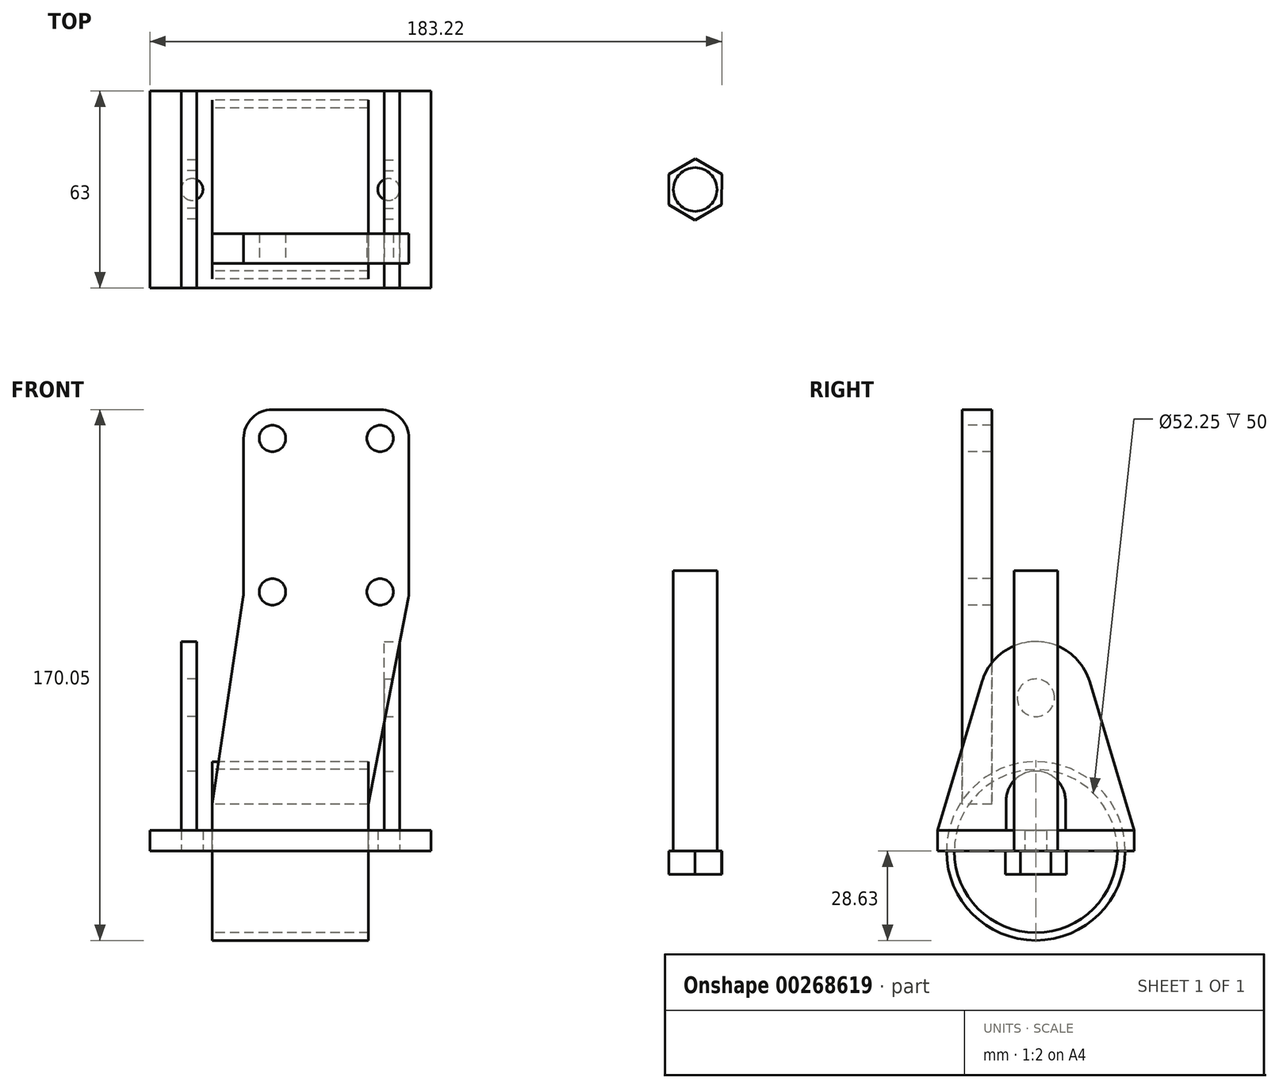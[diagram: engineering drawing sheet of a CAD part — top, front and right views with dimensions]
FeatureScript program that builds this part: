
annotation { "Feature Type Name" : "Feature", "Feature Type Description" : "" }
export const myFeature = defineFeature(function(context is Context, id is Id, definition is map)
    precondition{}
    {
        {
            var Q0;
            Q0=qCreatedBy(makeId("Top.planeOp"),FACE);
            var sketch = newSketch(context, id + "F0", { "sketchPlane" : qUnion([Q0])});
            skLineSegment(sketch, "E0.bottom", {"start": v(45, 31.5) * mm, "end": v(-45, 31.5) * mm});
            skLineSegment(sketch, "E0.top", {"start": v(45, -31.5) * mm, "end": v(-45, -31.5) * mm});
            skLineSegment(sketch, "E0.left", {"start": v(45, 31.5) * mm, "end": v(45, -31.5) * mm});
            skLineSegment(sketch, "E0.right", {"start": v(-45, 31.5) * mm, "end": v(-45, -31.5) * mm});
            skPoint(sketch, "E0.middle", {"position": v(0, 0) * mm});
            skCircle(sketch, "E1", {"center": v(31.5, 0) * mm, "radius": 3.5 * mm});
            skCircle(sketch, "E2.MirrorC", {"center": v(-31.5, 0) * mm, "radius": 3.5 * mm});
            skSolve(sketch);
        }
        {
            var Q0;
            Q0=makeQuery(id+"F0.imprint","IMPRINT",FACE,{"disambiguationData":[TD([[makeQuery(id+"F0.imprint","IMPRINT",EDGE,{"derivedFrom":sQuery(id+"F0.wireOp",EDGE,"E0.bottom")}),1.0]])]});
            extrude(context, id + "F1", {"entities" : qUnion([Q0]), "depth" : 6.6 * mm});
        }
        {
            var Q0;
            Q0=makeQuery(id+"F1.opExtrude","SWEPT_FACE",FACE,{"disambiguationData":[OSD([sQuery(id+"F0.wireOp",EDGE,"E0.right")])]});
            cPlane(context, id + "F2", {"entities" : qUnion([Q0]), "cplaneType" : CPlaneType.OFFSET, "offset" : 10 * mm, "oppositeDirection" : true, "width" : 150 * mm, "height" : 150 * mm});
        }
        {
            var Q0;
            Q0=qCreatedBy(id+"F2.planeOp",FACE);
            var sketch = newSketch(context, id + "F3", { "sketchPlane" : qUnion([Q0])});
            skLineSegment(sketch, "E3", {"start": v(-31.5, 6.6) * mm, "end": v(-9.5, 6.6) * mm});
            skCircle(sketch, "E4", {"center": v(0, 49.1) * mm, "radius": 6 * mm});
            skArc(sketch, "E5", {"start": v(17.25, 54.26) * mm, "mid": v(0, 67.1) * mm, "end": v(-17.25, 54.26) * mm});
            skLineSegment(sketch, "E6", {"start": v(31.5, 6.6) * mm, "end": v(17.25, 54.26) * mm});
            skLineSegment(sketch, "E7", {"start": v(-31.5, 6.6) * mm, "end": v(-17.25, 54.26) * mm});
            skLineSegment(sketch, "E8.left", {"start": v(9.5, 16.1) * mm, "end": v(9.5, 6.6) * mm});
            skLineSegment(sketch, "E8.right", {"start": v(-9.5, 16.1) * mm, "end": v(-9.5, 6.6) * mm});
            skPoint(sketch, "E8.middle", {"position": v(0, 6.6) * mm});
            skArc(sketch, "E9", {"start": v(9.5, 16.1) * mm, "mid": v(0, 25.6) * mm, "end": v(-9.5, 16.1) * mm});
            skLineSegment(sketch, "E10.trimOffspring", {"start": v(9.5, 6.6) * mm, "end": v(31.5, 6.6) * mm});
            skSolve(sketch);
        }
        {
            var Q0;
            Q0=makeQuery(id+"F3.imprint","IMPRINT",FACE,{"disambiguationData":[TD([[makeQuery(id+"F3.imprint","IMPRINT",EDGE,{"derivedFrom":sQuery(id+"F3.wireOp",EDGE,"E3")}),1.0]])]});
            extrude(context, id + "F4", {"entities" : qUnion([Q0]), "operationType" : NewBodyOperationType.ADD, "oppositeDirection" : true, "depth" : 5 * mm});
        }
        {
            var Q0;
            Q0=makeQuery(id+"F1.opExtrude","SWEPT_BODY",BODY,{"disambiguationData":[OSD([sQuery(id+"F0.wireOp",EDGE,"E0.bottom"),sQuery(id+"F0.wireOp",EDGE,"E0.top"),sQuery(id+"F0.wireOp",EDGE,"E0.left"),sQuery(id+"F0.wireOp",EDGE,"E0.right"),sQuery(id+"F0.wireOp",EDGE,"E1"),sQuery(id+"F0.wireOp",EDGE,"E2.MirrorC")])]});
            var Q1;
            Q1=qCreatedBy(makeId("Right.planeOp"),FACE);
            mirror(context, id + "F5", {"operationType" : NewBodyOperationType.ADD, "entities" : qUnion([Q0]), "mirrorPlane" : qUnion([Q1])});
        }
        {
            var Q0;
            Q0=qCreatedBy(makeId("Right.planeOp"),FACE);
            var sketch = newSketch(context, id + "F6", { "sketchPlane" : qUnion([Q0])});
            skCircle(sketch, "E11", {"center": v(0, 0) * mm, "radius": 28.62 * mm});
            skCircle(sketch, "E12", {"center": v(0, 0) * mm, "radius": 26.12 * mm});
            skSolve(sketch);
        }
        {
            var Q0;
            Q0=makeQuery(id+"F6.imprint","IMPRINT",FACE,{"disambiguationData":[TD([[makeQuery(id+"F6.imprint","IMPRINT",EDGE,{"derivedFrom":sQuery(id+"F6.wireOp",EDGE,"E11")}),1.0]])]});
            extrude(context, id + "F7", {"entities" : qUnion([Q0]), "endBound" : BoundingType.SYMMETRIC, "depth" : 50 * mm});
        }
        {
            var Q0;
            Q0=qCreatedBy(makeId("Front.planeOp"),FACE);
            cPlane(context, id + "F8", {"entities" : qUnion([Q0]), "cplaneType" : CPlaneType.OFFSET, "offset" : 23.62 * mm, "width" : 150 * mm, "height" : 150 * mm});
        }
        {
            var Q0;
            Q0=qCreatedBy(id+"F8.planeOp",FACE);
            var sketch = newSketch(context, id + "F9", { "sketchPlane" : qUnion([Q0])});
            skLineSegment(sketch, "E13.top", {"start": v(-5.75, 141.42) * mm, "end": v(28.75, 141.42) * mm});
            skLineSegment(sketch, "E13.left", {"start": v(-15, 82.91) * mm, "end": v(-15, 132.17) * mm});
            skLineSegment(sketch, "E13.right", {"start": v(38, 83.13) * mm, "end": v(38, 132.17) * mm});
            skPoint(sketch, "E13.middle", {"position": v(11.5, 111.8) * mm});
            skLineSegment(sketch, "E14", {"start": v(37.82, 81.23) * mm, "end": v(25, 15) * mm});
            skLineSegment(sketch, "E15", {"start": v(25, 15) * mm, "end": v(-25, 15) * mm});
            skLineSegment(sketch, "E16", {"start": v(-25, 15) * mm, "end": v(-15.1, 81.44) * mm});
            skPoint(sketch, "E17.visualSharp", {"position": v(38, 82.17) * mm});
            skArc(sketch, "E17.filletArc", {"start": v(37.82, 81.23) * mm, "mid": v(37.95, 82.18) * mm, "end": v(38, 83.13) * mm});
            skPoint(sketch, "E18.visualSharp", {"position": v(-15, 82.17) * mm});
            skArc(sketch, "E18.filletArc", {"start": v(-15.1, 81.44) * mm, "mid": v(-15.03, 82.17) * mm, "end": v(-15, 82.91) * mm});
            skCircle(sketch, "E19", {"center": v(28.75, 132.17) * mm, "radius": 4.25 * mm});
            skCircle(sketch, "E20", {"center": v(-5.75, 132.17) * mm, "radius": 4.25 * mm});
            skCircle(sketch, "E21", {"center": v(28.75, 83.02) * mm, "radius": 4.25 * mm});
            skCircle(sketch, "E22", {"center": v(-5.75, 83.02) * mm, "radius": 4.25 * mm});
            skPoint(sketch, "E23.visualSharp", {"position": v(-15, 141.42) * mm});
            skArc(sketch, "E23.filletArc", {"start": v(-5.75, 141.42) * mm, "mid": v(-12.3, 138.71) * mm, "end": v(-15, 132.17) * mm});
            skPoint(sketch, "E24.visualSharp", {"position": v(38, 141.42) * mm});
            skArc(sketch, "E24.filletArc", {"start": v(38, 132.17) * mm, "mid": v(35.3, 138.71) * mm, "end": v(28.75, 141.42) * mm});
            skSolve(sketch);
        }
        {
            var Q0;
            Q0=makeQuery(id+"F9.imprint","IMPRINT",FACE,{"disambiguationData":[TD([[makeQuery(id+"F9.imprint","IMPRINT",EDGE,{"derivedFrom":sQuery(id+"F9.wireOp",EDGE,"E13.top")}),-1.0]])]});
            extrude(context, id + "F10", {"entities" : qUnion([Q0]), "oppositeDirection" : true, "depth" : 9.5 * mm});
        }
        {
            var Q0;
            Q0=qCreatedBy(makeId("Top.planeOp"),FACE);
            var sketch = newSketch(context, id + "F11", { "sketchPlane" : qUnion([Q0])});
            skCircle(sketch, "E25", {"center": v(129.7, 0) * mm, "radius": 7 * mm});
            skSolve(sketch);
        }
        {
            var Q0;
            Q0=makeQuery(id+"F11.imprint","IMPRINT",FACE,{"disambiguationData":[TD([[makeQuery(id+"F11.imprint","IMPRINT",EDGE,{"derivedFrom":sQuery(id+"F11.wireOp",EDGE,"E25")}),1.0]])]});
            extrude(context, id + "F12", {"entities" : qUnion([Q0]), "depth" : (97.25 - 7.5) * mm});
        }
        {
            var Q0;
            Q0=makeQuery(id+"F12.opExtrude","CAP_FACE",FACE,{"disambiguationData":[OSD([sQuery(id+"F11.wireOp",EDGE,"E25")])],"isStart":true});
            var sketch = newSketch(context, id + "F13", { "sketchPlane" : qUnion([Q0])});
            skCircle(sketch, "E26.cCircle", {"center": v(129.7, 0) * mm, "radius": 8.5 * mm, "construction": true});
            skLineSegment(sketch, "E26.0", {"start": v(129.67, 9.81) * mm, "end": v(138.19, 4.93) * mm});
            skLineSegment(sketch, "E26.1", {"start": v(138.19, 4.93) * mm, "end": v(138.22, -4.88) * mm});
            skLineSegment(sketch, "E26.2", {"start": v(138.22, -4.88) * mm, "end": v(129.73, -9.81) * mm});
            skLineSegment(sketch, "E26.3", {"start": v(129.73, -9.81) * mm, "end": v(121.22, -4.93) * mm});
            skLineSegment(sketch, "E26.4", {"start": v(121.22, -4.93) * mm, "end": v(121.19, 4.88) * mm});
            skLineSegment(sketch, "E26.5", {"start": v(121.19, 4.88) * mm, "end": v(129.67, 9.81) * mm});
            skPoint(sketch, "E26.0.midPoint", {"position": v(133.93, 7.37) * mm});
            skSolve(sketch);
        }
        {
            var Q0;
            Q0=makeQuery(id+"F13.imprint","IMPRINT",FACE,{"disambiguationData":[TD([[makeQuery(id+"F13.imprint","IMPRINT",EDGE,{"derivedFrom":sQuery(id+"F13.wireOp",EDGE,"E26.0")}),-1.0]])]});
            var Q1;
            Q1=makeQuery(id+"F13.imprint","IMPRINT",FACE,{"disambiguationData":[TD([[makeQuery(id+"F13.imprint","IMPRINT",EDGE,{"derivedFrom":makeQuery(id+"F12.opExtrude","CAP_EDGE",EDGE,{"disambiguationData":[OSD([sQuery(id+"F11.wireOp",EDGE,"E25")])],"isStart":true})}),-1.0]])]});
            extrude(context, id + "F14", {"entities" : qUnion([Q0, Q1]), "operationType" : NewBodyOperationType.ADD, "depth" : 7.5 * mm});
        }
    });
